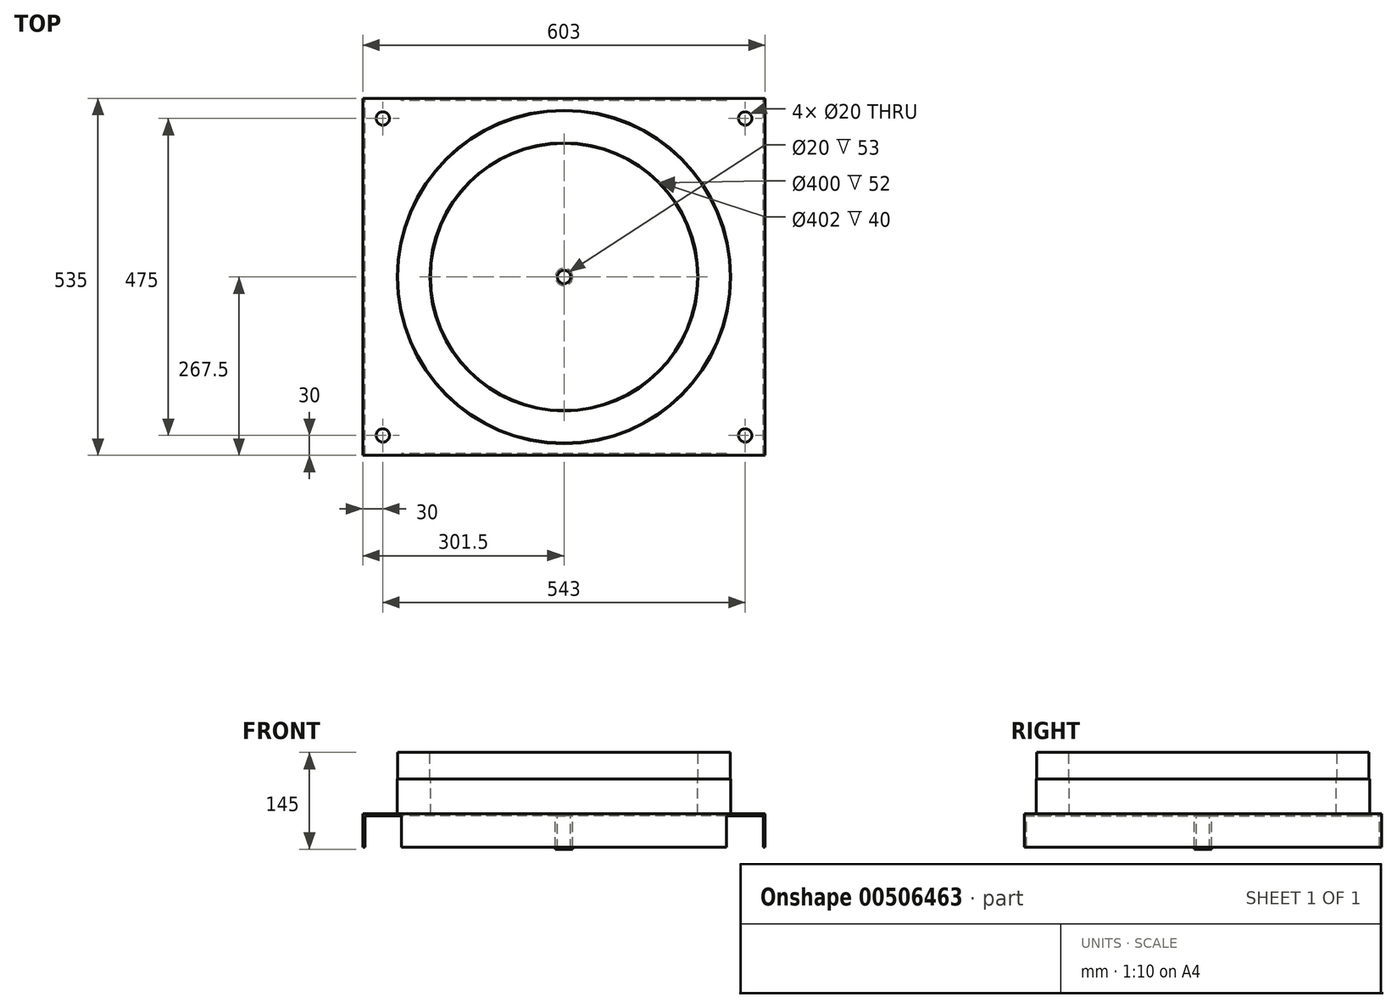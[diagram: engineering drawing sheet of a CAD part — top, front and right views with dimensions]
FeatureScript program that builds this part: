
annotation { "Feature Type Name" : "Feature", "Feature Type Description" : "" }
export const myFeature = defineFeature(function(context is Context, id is Id, definition is map)
    precondition{}
    {
        {
            var Q0;
            Q0=qCreatedBy(makeId("Front.planeOp"),FACE);
            var sketch = newSketch(context, id + "F0", { "sketchPlane" : qUnion([Q0])});
            skLineSegment(sketch, "E0", {"start": v(0, 74.87) * mm, "end": v(0, -73.71) * mm, "construction": true});
            skLineSegment(sketch, "E1", {"start": v(0, 374.84) * mm, "end": v(0, 1) * mm, "construction": true});
            skLineSegment(sketch, "E2", {"start": v(-200, 3) * mm, "end": v(-200, 55) * mm});
            skLineSegment(sketch, "E3", {"start": v(-200, 55) * mm, "end": v(-201, 55) * mm});
            skLineSegment(sketch, "E4", {"start": v(-201, 55) * mm, "end": v(-201, 95) * mm});
            skLineSegment(sketch, "E5", {"start": v(-201, 95) * mm, "end": v(-249, 95) * mm});
            skLineSegment(sketch, "E6", {"start": v(-249, 95) * mm, "end": v(-249, 55) * mm});
            skLineSegment(sketch, "E7", {"start": v(-249, 55) * mm, "end": v(-250, 55) * mm});
            skLineSegment(sketch, "E8", {"start": v(-250, 55) * mm, "end": v(-250, 3) * mm});
            skLineSegment(sketch, "E9", {"start": v(-250, 3) * mm, "end": v(-200, 3) * mm});
            skLineSegment(sketch, "E10.trimOffspring", {"start": v(0, 0) * mm, "end": v(0, -528.94) * mm, "construction": true});
            skLineSegment(sketch, "E11.bottom", {"start": v(-250, 3) * mm, "end": v(-10, 3) * mm});
            skLineSegment(sketch, "E11.top", {"start": v(-250, 0) * mm, "end": v(-10, 0) * mm});
            skLineSegment(sketch, "E11.left", {"start": v(-250, 3) * mm, "end": v(-250, 0) * mm});
            skLineSegment(sketch, "E11.right", {"start": v(-10, 3) * mm, "end": v(-10, 0) * mm});
            skSolve(sketch);
        }
        {
            var Q0;
            Q0=qSketchRegion(id+"F0",true);
            var Q1;
            Q1=sQuery(id+"F0.wireOp",EDGE,"E1");
            revolve(context, id + "F1", {"entities" : qUnion([Q0]), "axis" : qUnion([Q1]), "revolveType" : RevolveType.FULL});
        }
        {
            var Q0;
            Q0=qCreatedBy(makeId("Top.planeOp"),FACE);
            var sketch = newSketch(context, id + "F2", { "sketchPlane" : qUnion([Q0])});
            skLineSegment(sketch, "E12.bottom", {"start": v(301.5, 267.5) * mm, "end": v(-301.5, 267.5) * mm});
            skLineSegment(sketch, "E12.top", {"start": v(301.5, -267.5) * mm, "end": v(-301.5, -267.5) * mm});
            skLineSegment(sketch, "E12.left", {"start": v(301.5, 267.5) * mm, "end": v(301.5, -267.5) * mm});
            skLineSegment(sketch, "E12.right", {"start": v(-301.5, 267.5) * mm, "end": v(-301.5, -267.5) * mm});
            skPoint(sketch, "E12.middle", {"position": v(0, 0) * mm});
            skCircle(sketch, "E13.0", {"center": v(0, 0) * mm, "radius": 201 * mm});
            skCircle(sketch, "E14.0", {"center": v(0, 0) * mm, "radius": 200 * mm});
            skLineSegment(sketch, "E15", {"start": v(0, 0) * mm, "end": v(0, 773.78) * mm, "construction": true});
            skLineSegment(sketch, "E16", {"start": v(0, 0) * mm, "end": v(1007.48, 0) * mm, "construction": true});
            skCircle(sketch, "E17", {"center": v(271.5, 237.5) * mm, "radius": 10 * mm});
            skCircle(sketch, "E18.MirrorC", {"center": v(-271.5, 237.5) * mm, "radius": 10 * mm});
            skCircle(sketch, "E19.MirrorC", {"center": v(271.5, -237.5) * mm, "radius": 10 * mm});
            skCircle(sketch, "E20.MirrorC", {"center": v(-271.5, -237.5) * mm, "radius": 10 * mm});
            skSolve(sketch);
        }
        {
            var Q0;
            Q0=qSketchRegion(id+"F2",true);
            extrude(context, id + "F3", {"entities" : qUnion([Q0]), "operationType" : NewBodyOperationType.ADD, "depth" : 3 * mm, "offsetDistance" : 25 * mm});
        }
        {
            var Q0;
            Q0=makeQuery(id+"F3.opExtrude","CAP_FACE",FACE,{"disambiguationData":[OSD([sQuery(id+"F2.wireOp",EDGE,"E12.bottom"),sQuery(id+"F2.wireOp",EDGE,"E12.top"),sQuery(id+"F2.wireOp",EDGE,"E12.left"),sQuery(id+"F2.wireOp",EDGE,"E12.right"),sQuery(id+"F2.wireOp",EDGE,"E14.0"),sQuery(id+"F2.wireOp",EDGE,"E17"),sQuery(id+"F2.wireOp",EDGE,"E18.MirrorC"),sQuery(id+"F2.wireOp",EDGE,"E19.MirrorC"),sQuery(id+"F2.wireOp",EDGE,"E20.MirrorC")])],"isStart":false});
            var sketch = newSketch(context, id + "F4", { "sketchPlane" : qUnion([Q0])});
            skLineSegment(sketch, "E21", {"start": v(0, 0) * mm, "end": v(-1098.02, 0) * mm, "construction": true});
            skLineSegment(sketch, "E22", {"start": v(0, 0) * mm, "end": v(0, -1084.2) * mm, "construction": true});
            skLineSegment(sketch, "E23.bottom", {"start": v(-301.5, -267.5) * mm, "end": v(-298.5, -267.5) * mm});
            skLineSegment(sketch, "E23.top", {"start": v(-301.5, 267.5) * mm, "end": v(-298.5, 267.5) * mm});
            skLineSegment(sketch, "E23.left", {"start": v(-301.5, 267.5) * mm, "end": v(-301.5, -267.5) * mm});
            skLineSegment(sketch, "E23.right", {"start": v(-298.5, 267.5) * mm, "end": v(-298.5, -267.5) * mm});
            skLineSegment(sketch, "E24.MirrorCS", {"start": v(301.5, 267.5) * mm, "end": v(298.5, 267.5) * mm});
            skLineSegment(sketch, "E25.MirrorCS", {"start": v(301.5, -267.5) * mm, "end": v(298.5, -267.5) * mm});
            skLineSegment(sketch, "E26.MirrorCS", {"start": v(301.5, 267.5) * mm, "end": v(301.5, -267.5) * mm});
            skLineSegment(sketch, "E27.MirrorCS", {"start": v(298.5, 267.5) * mm, "end": v(298.5, -267.5) * mm});
            skLineSegment(sketch, "E28.MirrorCS", {"start": v(0, 0) * mm, "end": v(1098.02, 0) * mm, "construction": true});
            skLineSegment(sketch, "E29.bottom", {"start": v(-243.5, -267.5) * mm, "end": v(243.5, -267.5) * mm});
            skLineSegment(sketch, "E29.top", {"start": v(-243.5, -264.5) * mm, "end": v(243.5, -264.5) * mm});
            skLineSegment(sketch, "E29.left", {"start": v(-243.5, -267.5) * mm, "end": v(-243.5, -264.5) * mm});
            skLineSegment(sketch, "E29.right", {"start": v(243.5, -267.5) * mm, "end": v(243.5, -264.5) * mm});
            skLineSegment(sketch, "E30.MirrorCS", {"start": v(-243.5, 267.5) * mm, "end": v(-243.5, 264.5) * mm});
            skLineSegment(sketch, "E31.MirrorCS", {"start": v(243.5, 267.5) * mm, "end": v(243.5, 264.5) * mm});
            skLineSegment(sketch, "E32.MirrorCS", {"start": v(-243.5, 267.5) * mm, "end": v(243.5, 267.5) * mm});
            skLineSegment(sketch, "E33.MirrorCS", {"start": v(-243.5, 264.5) * mm, "end": v(243.5, 264.5) * mm});
            skSolve(sketch);
        }
        {
            var Q0;
            Q0=qSketchRegion(id+"F4",true);
            extrude(context, id + "F5", {"entities" : qUnion([Q0]), "operationType" : NewBodyOperationType.ADD, "oppositeDirection" : true, "depth" : 50 * mm, "offsetDistance" : 25 * mm});
        }
        {
            var Q0;
            Q0=makeQuery(id+"F3.boolean.opBoolean","MERGE",FACE,{"derivedFrom":[makeQuery(id+"F1.opRevolve","SWEPT_FACE",FACE,{"disambiguationData":[OSD([sQuery(id+"F0.wireOp",EDGE,"E11.top")])]}),makeQuery(id+"F3.opExtrude","CAP_FACE",FACE,{"disambiguationData":[OSD([sQuery(id+"F2.wireOp",EDGE,"E12.bottom"),sQuery(id+"F2.wireOp",EDGE,"E12.top"),sQuery(id+"F2.wireOp",EDGE,"E12.left"),sQuery(id+"F2.wireOp",EDGE,"E12.right"),sQuery(id+"F2.wireOp",EDGE,"E13.0"),sQuery(id+"F2.wireOp",EDGE,"E17"),sQuery(id+"F2.wireOp",EDGE,"E18.MirrorC"),sQuery(id+"F2.wireOp",EDGE,"E19.MirrorC"),sQuery(id+"F2.wireOp",EDGE,"E20.MirrorC")])],"isStart":false})]});
            var sketch = newSketch(context, id + "F6", { "sketchPlane" : qUnion([Q0])});
            skCircle(sketch, "E34.0", {"center": v(0, 0) * mm, "radius": 10 * mm});
            skCircle(sketch, "E35", {"center": v(0, 0) * mm, "radius": 13 * mm});
            skSolve(sketch);
        }
        {
            var Q0;
            Q0=qSketchRegion(id+"F6",true);
            extrude(context, id + "F7", {"entities" : qUnion([Q0]), "operationType" : NewBodyOperationType.ADD, "depth" : 50 * mm, "offsetDistance" : 25 * mm});
        }
    });
